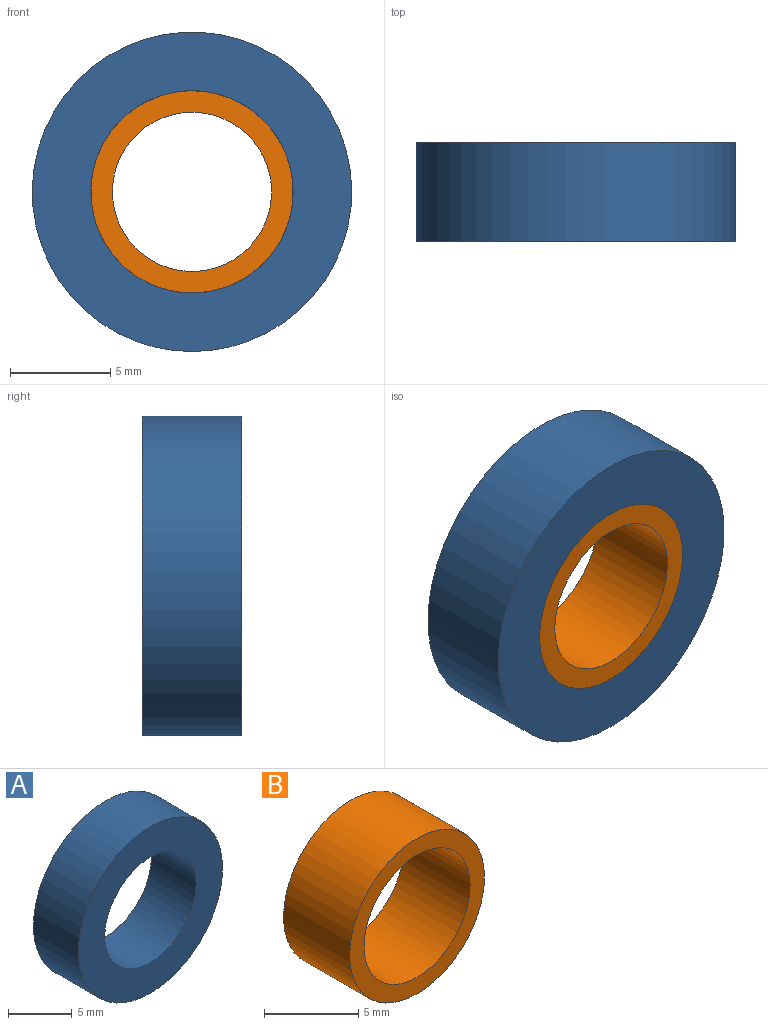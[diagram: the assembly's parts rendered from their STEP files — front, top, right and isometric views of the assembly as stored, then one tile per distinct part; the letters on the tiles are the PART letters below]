
ASSEMBLY  parts=2 mates=1
PART A: 4 faces, bbox 16x5x16 mm
  f0: plane 15.95x15.95mm, normal (0,1,0), area 119.7mm2, adj f1,f3
  f1: cylinder r=7.97mm len=15.95mm, axis (0,-1,0), area 248.5mm2, adj f0,f2
  f2: plane 15.95x15.95mm, normal (0,-1,0), area 119.7mm2, adj f1,f3
  f3: cylinder r=5.05mm len=10.1mm, axis (0,-1,0), area 157.4mm2, adj f0,f2
PART B: 4 faces, bbox 10.1x5x10.1 mm
  f0: plane 10.1x10.1mm, normal (0,1,0), area 30.5mm2, adj f1,f3
  f1: cylinder r=5.05mm len=10.1mm, axis (0,-1,0), area 157.4mm2, adj f0,f2
  f2: plane 10.1x10.1mm, normal (0,-1,0), area 30.5mm2, adj f1,f3
  f3: cylinder r=3.98mm len=7.95mm, axis (0,-1,0), area 123.9mm2, adj f0,f2
PLACE A t=(0,-2.48,0)mm
PLACE B rot(axis=(0,1,0),81deg) t=(0,-2.48,0)mm
MATE revolute B.f1 <-> A.f1  axis (0,-1,0) through (0,-4.96,0)mm
